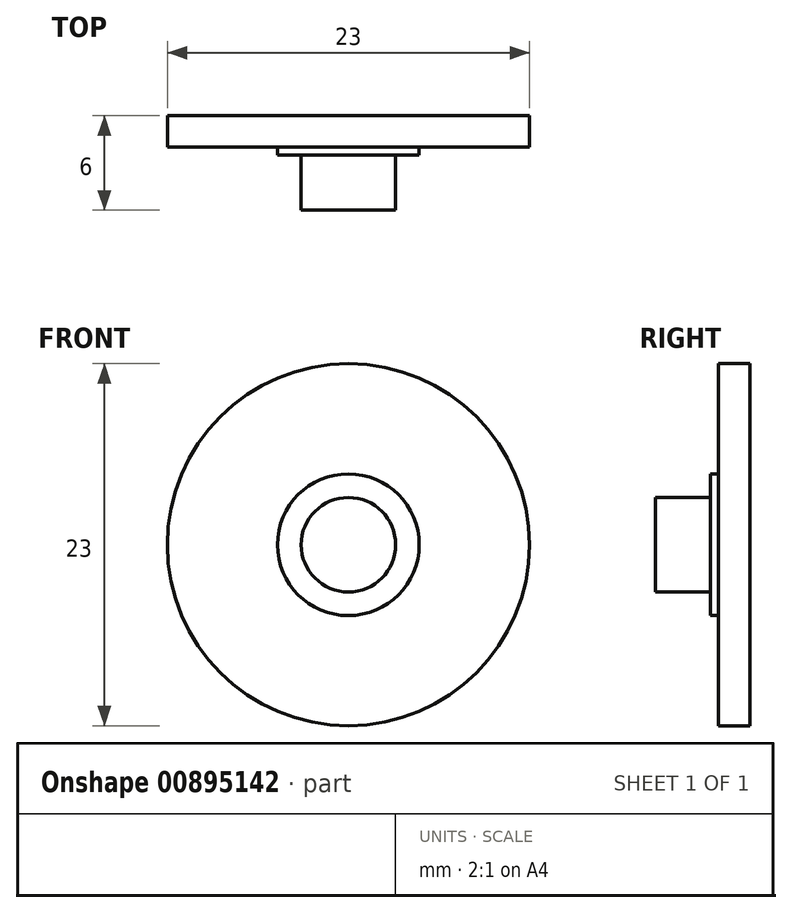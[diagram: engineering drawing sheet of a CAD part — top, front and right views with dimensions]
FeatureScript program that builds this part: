
annotation { "Feature Type Name" : "Feature", "Feature Type Description" : "" }
export const myFeature = defineFeature(function(context is Context, id is Id, definition is map)
    precondition{}
    {
        {
            var Q0;
            Q0=qCreatedBy(makeId("Front.planeOp"),FACE);
            var sketch = newSketch(context, id + "F0", { "sketchPlane" : qUnion([Q0])});
            skCircle(sketch, "E0", {"center": v(0, 0) * mm, "radius": 11.5 * mm});
            skCircle(sketch, "E1", {"center": v(0, 0) * mm, "radius": 4.5 * mm});
            skCircle(sketch, "E2", {"center": v(0, 0) * mm, "radius": 3 * mm});
            skSolve(sketch);
        }
        {
            var Q0;
            Q0=makeQuery(id+"F0.imprint","IMPRINT",FACE,{"disambiguationData":[TD([[makeQuery(id+"F0.imprint","IMPRINT",EDGE,{"derivedFrom":sQuery(id+"F0.wireOp",EDGE,"E2")}),1.0]])]});
            var Q1;
            Q1=makeQuery(id+"F0.imprint","IMPRINT",FACE,{"disambiguationData":[TD([[makeQuery(id+"F0.imprint","IMPRINT",EDGE,{"derivedFrom":sQuery(id+"F0.wireOp",EDGE,"E1")}),1.0]])]});
            var Q2;
            Q2=makeQuery(id+"F0.imprint","IMPRINT",FACE,{"disambiguationData":[TD([[makeQuery(id+"F0.imprint","IMPRINT",EDGE,{"derivedFrom":sQuery(id+"F0.wireOp",EDGE,"E0")}),1.0]])]});
            extrude(context, id + "F1", {"entities" : qUnion([Q0, Q1, Q2]), "depth" : 2 * mm, "offsetDistance" : 25 * mm});
        }
        {
            var Q0;
            Q0=makeQuery(id+"F0.imprint","IMPRINT",FACE,{"disambiguationData":[TD([[makeQuery(id+"F0.imprint","IMPRINT",EDGE,{"derivedFrom":sQuery(id+"F0.wireOp",EDGE,"E1")}),1.0]])]});
            extrude(context, id + "F2", {"entities" : qUnion([Q0]), "operationType" : NewBodyOperationType.ADD, "depth" : 2.5 * mm, "offsetDistance" : 25 * mm});
        }
        {
            var Q0;
            Q0=makeQuery(id+"F0.imprint","IMPRINT",FACE,{"disambiguationData":[TD([[makeQuery(id+"F0.imprint","IMPRINT",EDGE,{"derivedFrom":sQuery(id+"F0.wireOp",EDGE,"E2")}),1.0]])]});
            extrude(context, id + "F3", {"entities" : qUnion([Q0]), "operationType" : NewBodyOperationType.ADD, "depth" : 6 * mm, "offsetDistance" : 25 * mm});
        }
    });
